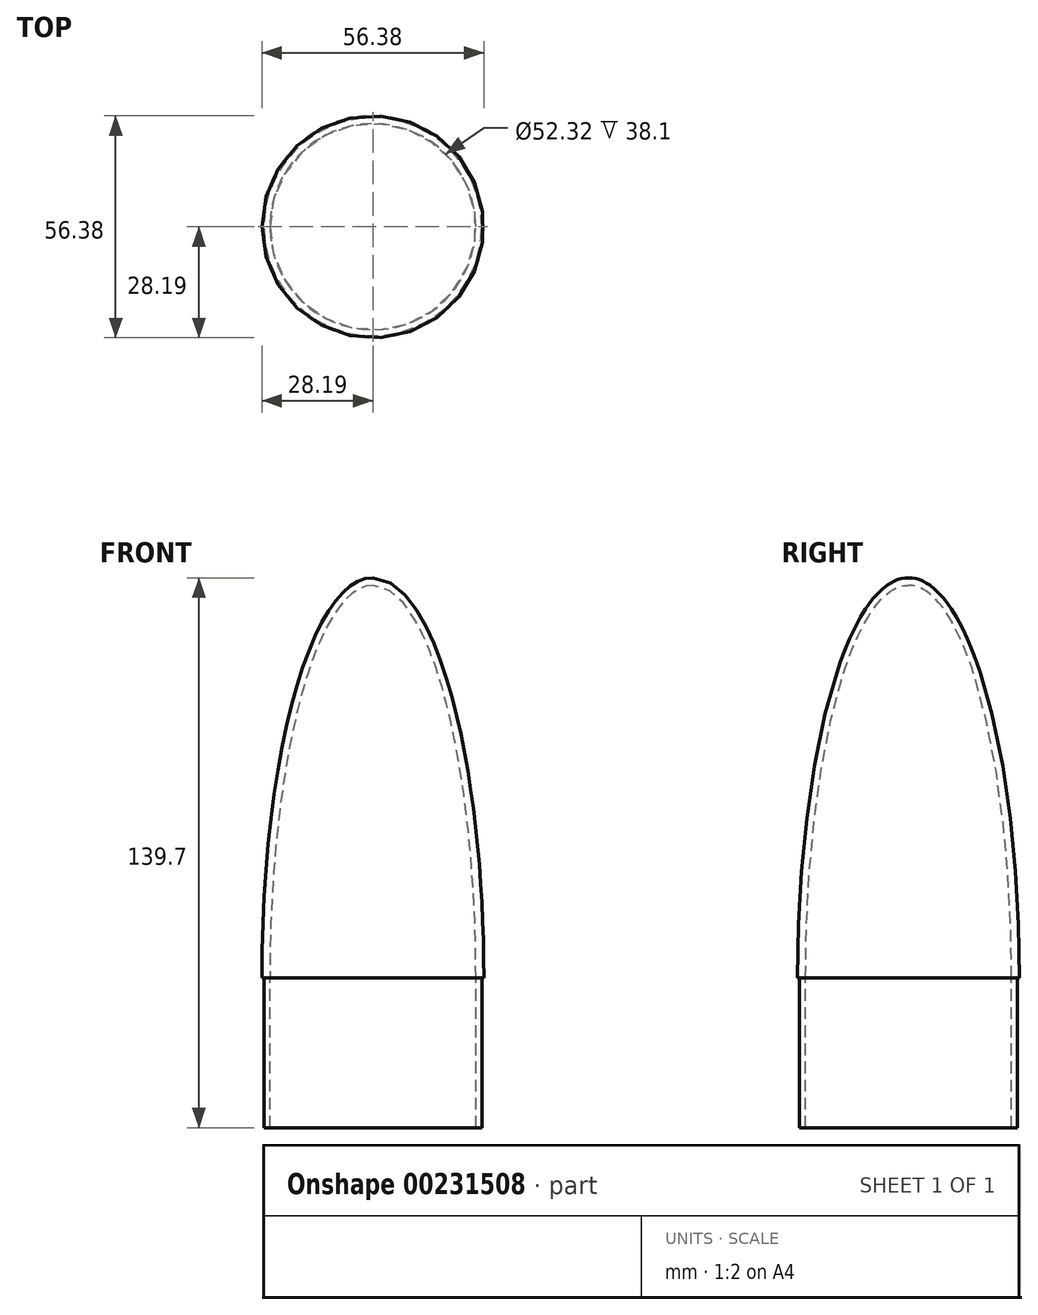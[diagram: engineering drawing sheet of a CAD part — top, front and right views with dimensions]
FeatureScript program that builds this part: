
annotation { "Feature Type Name" : "Feature", "Feature Type Description" : "" }
export const myFeature = defineFeature(function(context is Context, id is Id, definition is map)
    precondition{}
    {
        {
            var Q0;
            Q0=qCreatedBy(makeId("Front.planeOp"),FACE);
            var sketch = newSketch(context, id + "F0", { "sketchPlane" : qUnion([Q0])});
            skLineSegment(sketch, "E0", {"start": v(0, 0) * mm, "end": v(0, 101.6) * mm, "construction": true});
            skLineSegment(sketch, "E1", {"start": v(0, 0) * mm, "end": v(28.2, 0) * mm, "construction": true});
            skEllipse(sketch, "E2", {"center": v(0, 0) * mm, "majorRadius": 101.6 * mm, "minorRadius": 28.2 * mm, "majorAxis": v(0, 1)});
            skPoint(sketch, "E3", {"position": v(26.16, 0) * mm});
            skPoint(sketch, "E4", {"position": v(0, 99.7) * mm});
            skEllipse(sketch, "E5", {"center": v(0, 0) * mm, "majorRadius": 99.7 * mm, "minorRadius": 26.16 * mm, "majorAxis": v(0, 1)});
            skLineSegment(sketch, "E6", {"start": v(-28.2, 0) * mm, "end": v(28.2, 0) * mm});
            skLineSegment(sketch, "E7", {"start": v(0, 101.6) * mm, "end": v(0, 0) * mm});
            skSolve(sketch);
        }
        {
            var Q0;
            {var subQ0=sQuery(id+"F0.wireOp",EDGE,"E6");var subQ1=sQuery(id+"F0.wireOp",EDGE,"E2");var subQ2=makeQuery(id+"F0.imprint","INTERSECT",VERTEX,{"disambiguationData":[OD(0.0)],"derivedFrom":[subQ1,subQ0]});Q0=makeQuery(id+"F0.imprint","IMPRINT",FACE,{"disambiguationData":[TD([[makeQuery(id+"F0.imprint","IMPRINT",EDGE,{"disambiguationData":[TD([[subQ2,1.0]])],"derivedFrom":subQ1}),1.0]])]});}
            var Q1;
            Q1=sQuery(id+"F0.wireOp",EDGE,"E0");
            revolve(context, id + "F1", {"surfaceOperationType" : NewSurfaceOperationType.NEW, "entities" : qUnion([Q0]), "axis" : qUnion([Q1]), "revolveType" : RevolveType.FULL});
        }
        {
            var Q0;
            Q0=qCreatedBy(makeId("Front.planeOp"),FACE);
            var sketch = newSketch(context, id + "F2", { "sketchPlane" : qUnion([Q0])});
            skLineSegment(sketch, "E8", {"start": v(0, 0) * mm, "end": v(0, -38.1) * mm, "construction": true});
            skLineSegment(sketch, "E9", {"start": v(0, 0) * mm, "end": v(-27.69, 0) * mm, "construction": true});
            skEllipse(sketch, "E10.0", {"center": v(0, 0) * mm, "majorRadius": 99.7 * mm, "minorRadius": 26.16 * mm, "majorAxis": v(0, 1)});
            skPoint(sketch, "E11", {"position": v(-26.16, 0) * mm});
            skLineSegment(sketch, "E12", {"start": v(-27.69, 0) * mm, "end": v(-27.69, -38.1) * mm});
            skLineSegment(sketch, "E13", {"start": v(-27.69, -38.1) * mm, "end": v(-26.16, -38.1) * mm});
            skLineSegment(sketch, "E14", {"start": v(-26.16, -38.1) * mm, "end": v(-26.16, 0) * mm});
            skLineSegment(sketch, "E15", {"start": v(-27.69, 0) * mm, "end": v(-26.16, 0) * mm});
            skSolve(sketch);
        }
        {
            var Q0;
            Q0=makeQuery(id+"F2.imprint","IMPRINT",FACE,{"disambiguationData":[TD([[makeQuery(id+"F2.imprint","IMPRINT",EDGE,{"derivedFrom":sQuery(id+"F2.wireOp",EDGE,"E12")}),1.0]])]});
            var Q1;
            Q1=sQuery(id+"F2.wireOp",EDGE,"E8");
            revolve(context, id + "F3", {"operationType" : NewBodyOperationType.ADD, "surfaceOperationType" : NewSurfaceOperationType.NEW, "entities" : qUnion([Q0]), "axis" : qUnion([Q1]), "revolveType" : RevolveType.FULL});
        }
    });
